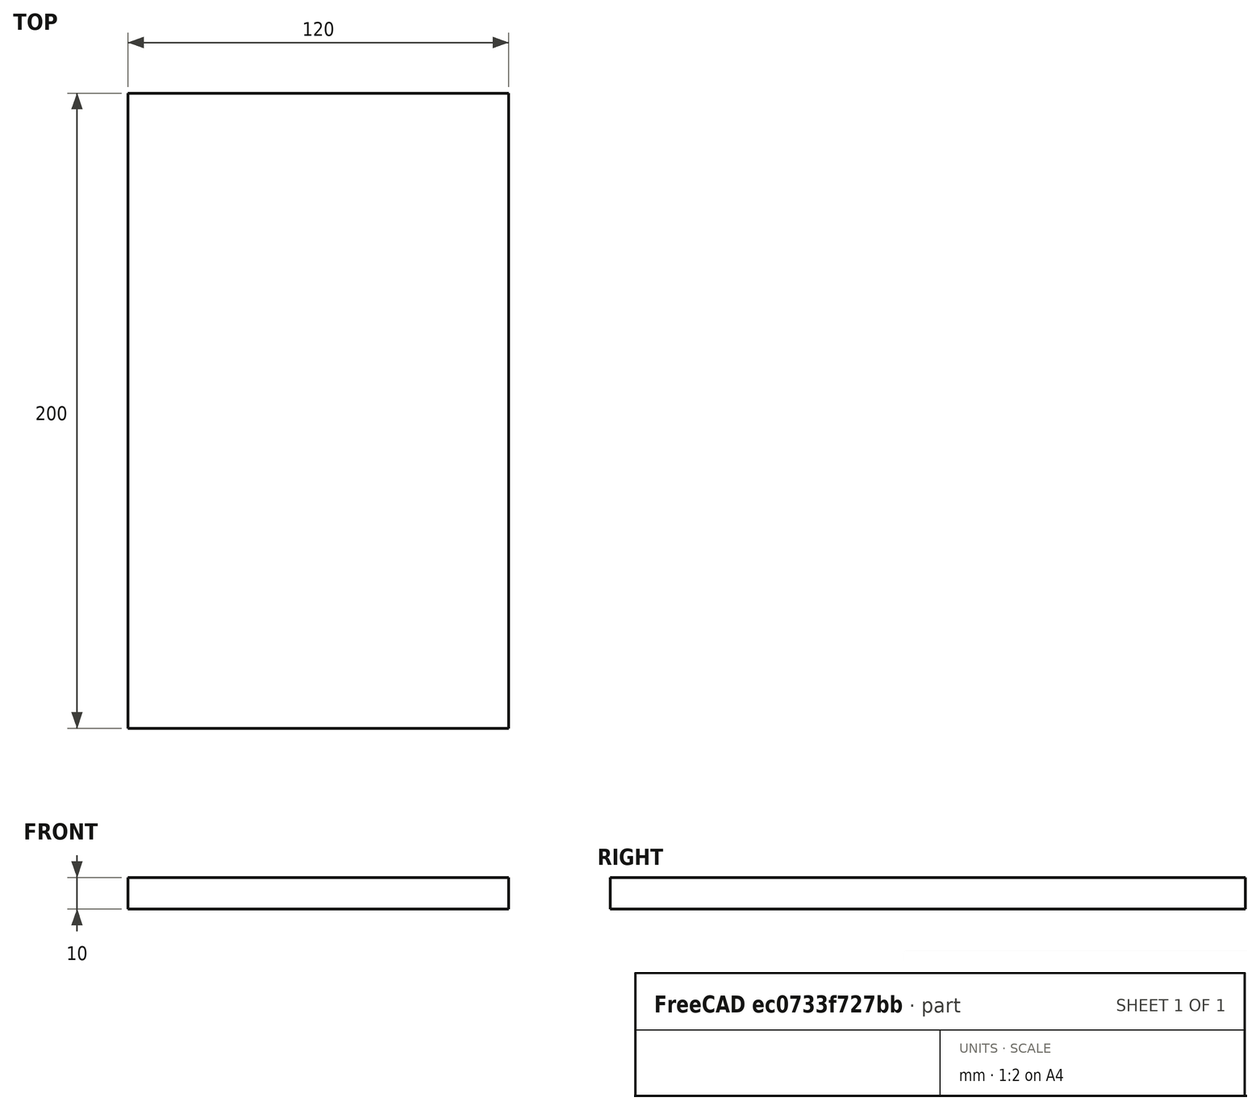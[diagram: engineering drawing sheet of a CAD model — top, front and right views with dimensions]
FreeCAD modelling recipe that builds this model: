
FCSTD DOCUMENT  (FreeCAD 0.16R6703 (Git))
Label: box_sides
License: All rights reserved
LicenseURL: http://en.wikipedia.org/wiki/All_rights_reserved
objects: Sketcher::SketchObject×1, PartDesign::Pad×1
note: 3 computed .brp shape members not serialized (recipe doc carries the construction recipe); baked Part::Feature solids carry a one-line shape summary decoded from their .brp

FEATURE [Sketcher::SketchObject] Sketch
  sketch-geometry (4):
    g0: LineSegment StartX=0 StartY=0 StartZ=0 EndX=120 EndY=0 EndZ=0
    g1: LineSegment StartX=120 StartY=0 StartZ=0 EndX=120 EndY=200 EndZ=0
    g2: LineSegment StartX=120 StartY=200 StartZ=0 EndX=0 EndY=200 EndZ=0
    g3: LineSegment StartX=0 StartY=200 StartZ=0 EndX=0 EndY=0 EndZ=0
  constraints (11):
    c: Coincident(g0,g1)
    c: Coincident(g1,g2)
    c: Coincident(g2,g3)
    c: Coincident(g3,g0)
    c: Horizontal(g0)
    c: Horizontal(g2)
    c: Vertical(g1)
    c: Vertical(g3)
    c: Coincident(g0,g-1)
    c: Distance(g0) = 120
    c: Distance(g1) = 200
FEATURE [PartDesign::Pad] Pad
  Length = 10
  Length2 = 100
  Sketch = -> Sketch
  Type = 0
